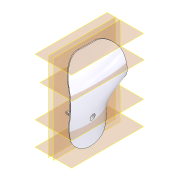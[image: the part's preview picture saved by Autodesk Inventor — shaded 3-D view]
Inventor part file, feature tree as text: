
AUTODESK INVENTOR PART (.ipt)
format: ipt  version: 2020.2 (Build 242310000, 310)  size: 365,056 bytes
history: native  units: mm
features: sketch x8, plane x6, extrude x3, loft x1, fillet x1
ambient origin geometry x8: Origin, YZ Plane, XZ Plane, XY Plane, X Axis, Y Axis, Z Axis, Center Point
bodies: Body1 (feature_tree)
feature tree (19):
  sketch  "Sketch1"  dims[d2=1.0mm d3=40.0mm d4=1.0mm]
  plane  "Work Plane1"
  sketch  "Sketch2"  dims[d5=-20.0mm d6=1.0mm]
  plane  "Work Plane2"
  sketch  "Sketch3"  dims[d13=-25.0mm d14=1.0mm]
  plane  "Work Plane3"
  plane  "Work Plane4"
  loft  "Loft2"
  fillet  "Fillet2"  Radius=1.0mm
  plane  "Work Plane6"
  extrude  "Extrusion4"  Depth=1.0mm
  plane  "Work Plane7"
  extrude  "Extrusion5"  Depth=1.0mm
  extrude  "Extrusion6"  Depth=15.0mm
  sketch  "Sketch4"  dims[d15=10.0mm d16=90.0deg d17=0.0mm d18=90.0deg d19=0.0mm d20=90.0deg d21=0.0mm d22=90.0deg d30=15.0mm]
  sketch  "Sketch6"  dims[d31=1.0mm]
  sketch  "Sketch9"  dims[d32=0.0mm d33=90.0deg]
  sketch  "Sketch10"  dims[d34=20.0mm]
  sketch  "Sketch11"  dims[d42=6.0mm d43=9.0mm d44=9.0mm d45=3.0mm d46=22.303mm d47=0.0mm d48=5.0mm d49=6.0mm d50=17.303mm d51=0.0mm d52=0.2mm d53=2.0mm d54=2.0mm d55=3.0mm d56=0.2mm d57=2.0mm d58=2.0mm d59=3.0mm d60=2.0mm d61=0.0mm]
